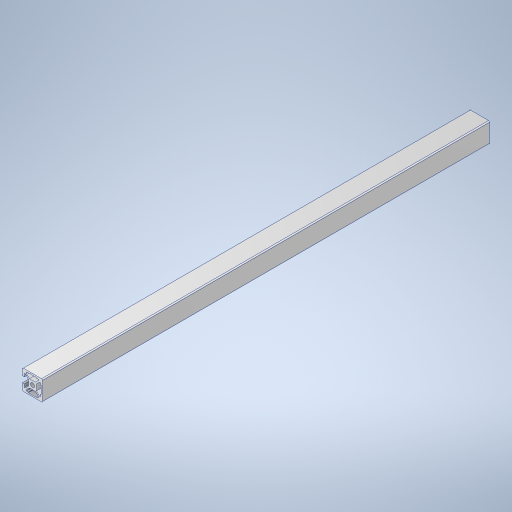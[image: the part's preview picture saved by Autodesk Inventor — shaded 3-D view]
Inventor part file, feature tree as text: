
AUTODESK INVENTOR PART (.ipt)
format: ipt  version: 2024 (Build 280153000, 153)  size: 363,008 bytes
history: native  units: mm
features: other x7, thread x2, sketch x2, extrude x1, hole x1
ambient origin geometry x8: Origin, YZ Plane, XZ Plane, XY Plane, X Axis, Y Axis, Z Axis, Center Point
bodies: Solid1 (feature_tree)
feature tree (13):
  extrude  "Extrusion1"  TaperAngle=0.0deg  [1 undecoded]
  hole  "Hole1"  [1 undecoded]
  other  "C1_XY"
  other  "C1_YZ"
  other  "C1_ZX"
  other  "C1_X"
  other  "C1_Y"
  other  "C1_Z"
  other  "C1_Center"
  thread  "Thread1"  [1 undecoded]
  thread  "Thread2"  [1 undecoded]
  sketch  "Sketch_66"  dims[d2=4.2mm d3=0.599mm d4=4.0mm d5=2.0mm d6=90.0deg d7=0.998mm d8=0.0mm d9=0.0mm d10=10.0mm d11=0.0mm d12=10.0mm d13=0.0mm]
  sketch  "Sketch2"  dims[d0=443.0mm d1=0.0mm]
note: 4 required parameter values undecoded (feature->parameter linkage not recoverable at this tier; creation-order binding heuristic only, values carry confidence <= 0.55)
